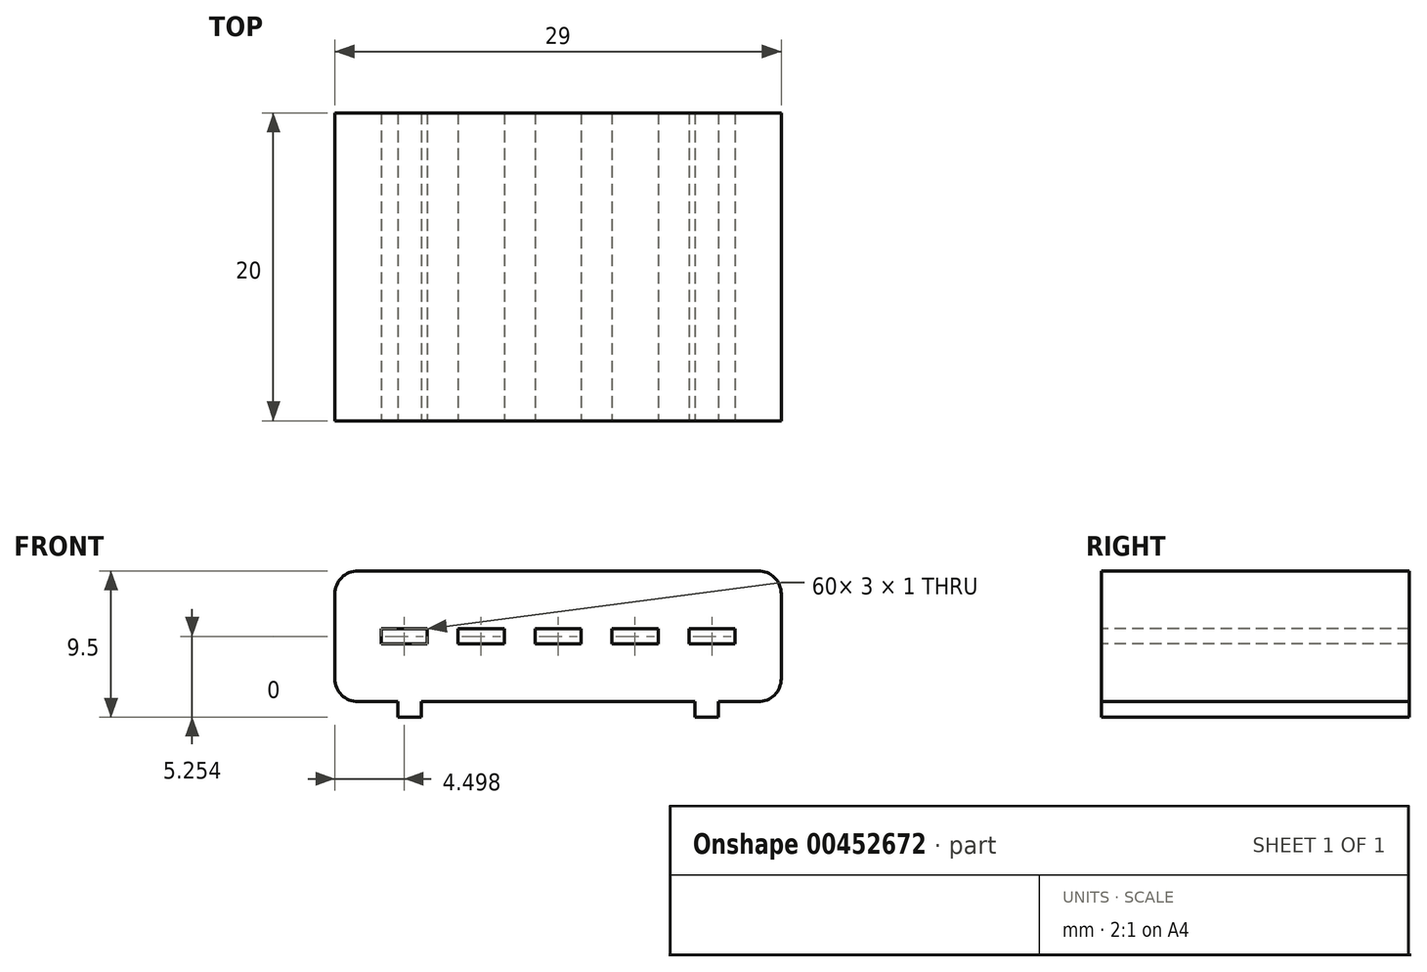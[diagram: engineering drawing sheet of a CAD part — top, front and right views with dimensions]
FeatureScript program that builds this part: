
annotation { "Feature Type Name" : "Feature", "Feature Type Description" : "" }
export const myFeature = defineFeature(function(context is Context, id is Id, definition is map)
    precondition{}
    {
        {
            var Q0;
            Q0=qCreatedBy(makeId("Front.planeOp"),FACE);
            var sketch = newSketch(context, id + "F0", { "sketchPlane" : qUnion([Q0])});
            skLineSegment(sketch, "E0.bottom", {"start": v(-11.47, -2.46) * mm, "end": v(14.53, -2.46) * mm});
            skLineSegment(sketch, "E0.top", {"start": v(-11.47, -10.96) * mm, "end": v(-8.87, -10.96) * mm});
            skLineSegment(sketch, "E0.left", {"start": v(-12.97, -3.96) * mm, "end": v(-12.97, -9.46) * mm});
            skLineSegment(sketch, "E0.right", {"start": v(16.03, -3.96) * mm, "end": v(16.03, -9.46) * mm});
            skLineSegment(sketch, "E1.bottom", {"start": v(-9.97, -6.2) * mm, "end": v(-6.97, -6.2) * mm});
            skLineSegment(sketch, "E1.top", {"start": v(-9.97, -7.2) * mm, "end": v(-6.97, -7.2) * mm});
            skLineSegment(sketch, "E1.left", {"start": v(-9.97, -6.2) * mm, "end": v(-9.97, -7.2) * mm});
            skLineSegment(sketch, "E1.right", {"start": v(-6.97, -6.2) * mm, "end": v(-6.97, -7.2) * mm});
            skPoint(sketch, "E2.oppositeSnap0", {"position": v(-8.47, -7.2) * mm});
            skLineSegment(sketch, "E2.bottom", {"start": v(-4.97, -6.2) * mm, "end": v(-1.97, -6.2) * mm});
            skLineSegment(sketch, "E2.top", {"start": v(-4.97, -7.2) * mm, "end": v(-1.97, -7.2) * mm});
            skLineSegment(sketch, "E2.left", {"start": v(-4.97, -6.2) * mm, "end": v(-4.97, -7.2) * mm});
            skLineSegment(sketch, "E2.right", {"start": v(-1.97, -6.2) * mm, "end": v(-1.97, -7.2) * mm});
            skLineSegment(sketch, "E3.bottom", {"start": v(5.03, -6.2) * mm, "end": v(8.03, -6.2) * mm});
            skLineSegment(sketch, "E3.top", {"start": v(5.03, -7.2) * mm, "end": v(8.03, -7.2) * mm});
            skLineSegment(sketch, "E3.left", {"start": v(5.03, -6.2) * mm, "end": v(5.03, -7.2) * mm});
            skLineSegment(sketch, "E3.right", {"start": v(8.03, -6.2) * mm, "end": v(8.03, -7.2) * mm});
            skLineSegment(sketch, "E4.bottom", {"start": v(10.03, -6.2) * mm, "end": v(13.03, -6.2) * mm});
            skLineSegment(sketch, "E4.top", {"start": v(10.03, -7.2) * mm, "end": v(13.03, -7.2) * mm});
            skLineSegment(sketch, "E4.left", {"start": v(10.03, -6.2) * mm, "end": v(10.03, -7.2) * mm});
            skLineSegment(sketch, "E4.right", {"start": v(13.03, -6.2) * mm, "end": v(13.03, -7.2) * mm});
            skLineSegment(sketch, "E5.bottom", {"start": v(0.03, -6.2) * mm, "end": v(3.03, -6.2) * mm});
            skLineSegment(sketch, "E5.top", {"start": v(0.03, -7.2) * mm, "end": v(3.03, -7.2) * mm});
            skLineSegment(sketch, "E5.left", {"start": v(0.03, -6.2) * mm, "end": v(0.03, -7.2) * mm});
            skLineSegment(sketch, "E5.right", {"start": v(3.03, -6.2) * mm, "end": v(3.03, -7.2) * mm});
            skPoint(sketch, "E6.visualSharp", {"position": v(-12.97, -2.46) * mm});
            skArc(sketch, "E6.filletArc", {"start": v(-11.47, -2.46) * mm, "mid": v(-12.53, -2.9) * mm, "end": v(-12.97, -3.96) * mm});
            skPoint(sketch, "E7.visualSharp", {"position": v(-12.97, -10.96) * mm});
            skArc(sketch, "E7.filletArc", {"start": v(-12.97, -9.46) * mm, "mid": v(-12.53, -10.52) * mm, "end": v(-11.47, -10.96) * mm});
            skPoint(sketch, "E8.visualSharp", {"position": v(16.03, -2.46) * mm});
            skArc(sketch, "E8.filletArc", {"start": v(16.03, -3.96) * mm, "mid": v(15.59, -2.9) * mm, "end": v(14.53, -2.46) * mm});
            skPoint(sketch, "E9.visualSharp", {"position": v(16.03, -10.96) * mm});
            skArc(sketch, "E9.filletArc", {"start": v(14.53, -10.96) * mm, "mid": v(15.59, -10.52) * mm, "end": v(16.03, -9.46) * mm});
            skLineSegment(sketch, "E10.top", {"start": v(-8.87, -11.96) * mm, "end": v(-7.37, -11.96) * mm});
            skLineSegment(sketch, "E10.left", {"start": v(-8.87, -10.96) * mm, "end": v(-8.87, -11.96) * mm});
            skLineSegment(sketch, "E10.right", {"start": v(-7.37, -10.96) * mm, "end": v(-7.37, -11.96) * mm});
            skLineSegment(sketch, "E11.top", {"start": v(10.43, -11.96) * mm, "end": v(11.93, -11.96) * mm});
            skLineSegment(sketch, "E11.left", {"start": v(10.43, -10.96) * mm, "end": v(10.43, -11.96) * mm});
            skLineSegment(sketch, "E11.right", {"start": v(11.93, -10.96) * mm, "end": v(11.93, -11.96) * mm});
            skPoint(sketch, "E12.startSnap0", {"position": v(1.53, -2.46) * mm});
            skLineSegment(sketch, "E13.trimOffspring", {"start": v(-7.37, -10.96) * mm, "end": v(10.43, -10.96) * mm});
            skLineSegment(sketch, "E14.trimOffspring", {"start": v(11.93, -10.96) * mm, "end": v(14.53, -10.96) * mm});
            skSolve(sketch);
        }
        {
            var Q0;
            Q0=makeQuery(id+"F0.imprint","IMPRINT",FACE,{"disambiguationData":[TD([[makeQuery(id+"F0.imprint","IMPRINT",EDGE,{"derivedFrom":sQuery(id+"F0.wireOp",EDGE,"E0.bottom")}),-1.0]])]});
            extrude(context, id + "F1", {"entities" : qUnion([Q0]), "oppositeDirection" : true, "depth" : 20 * mm});
        }
    });
